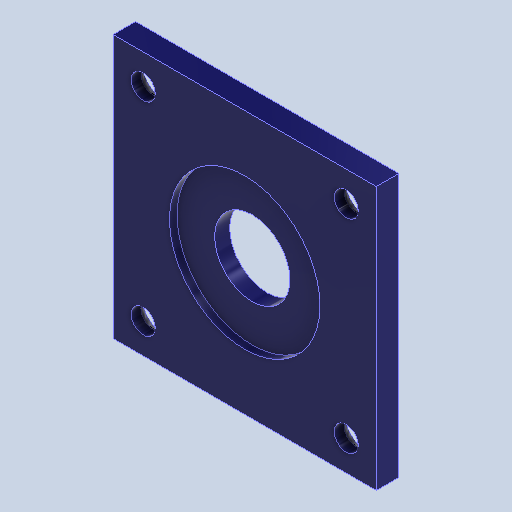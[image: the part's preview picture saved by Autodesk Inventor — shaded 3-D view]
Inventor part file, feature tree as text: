
AUTODESK INVENTOR PART (.ipt)
format: ipt  version: 2022 (Build 260153000, 153)  size: 151,040 bytes
history: native  units: mm
features: sketch x2, extrude x2, hole x1
ambient origin geometry x8: Origin, YZ Plane, XZ Plane, XY Plane, X Axis, Y Axis, Z Axis, Center Point
bodies: Solid1 (feature_tree)
feature tree (5):
  sketch  "Sketch1"  dims[d0=35.0mm d1=35.0mm]
  extrude  "Extrusion1"  Depth=35.0mm
  extrude  "Extrusion2"  Depth=2.0mm TaperAngle=360.0deg
  hole  "Hole2"  [1 undecoded]
  sketch  "Sketch2"  dims[d3=3.0mm d4=40.0mm d6=360.0deg d8=10.0mm d9=20.0mm d10=3.0mm d11=0.0mm d12=1.0mm d13=0.0mm d21=3.2mm d22=6.0mm d23=6.6mm d24=2.0mm d25=90.0deg d26=8.0mm d27=20.594885mm]
note: 1 required parameter value undecoded (feature->parameter linkage not recoverable at this tier; creation-order binding heuristic only, values carry confidence <= 0.55)
